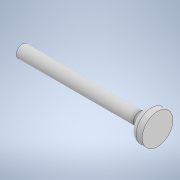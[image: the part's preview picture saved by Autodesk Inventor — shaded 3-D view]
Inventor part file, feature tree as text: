
AUTODESK INVENTOR PART (.ipt)
format: ipt  version: 2022 (Build 260153000, 153)  size: 117,248 bytes
history: native  units: in
note: dims shown in document units (in); Inventor stores cm internally (conversion verified against a paired STEP export)
features: extrude x2, fillet x2, sketch x2
ambient origin geometry x8: Origin, YZ Plane, XZ Plane, XY Plane, X Axis, Y Axis, Z Axis, Center Point
bodies: Solid1 (feature_tree)
feature tree (6):
  extrude  "Extrusion1"  Depth=7.874in TaperAngle=0.0deg
  extrude  "Extrusion2"  Depth=0.7874in TaperAngle=0.0deg
  fillet  "Fillet1"  Radius=0.3937in
  fillet  "Fillet2"  Radius=0.3937in
  sketch  "Sketch1"  dims[d0=0.7874in d1=7.874in d2=0.0in]
  sketch  "Sketch2"  dims[d3=1.9685in d4=0.7874in d5=0.0in d6=0.3937in d7=0.3937in]
